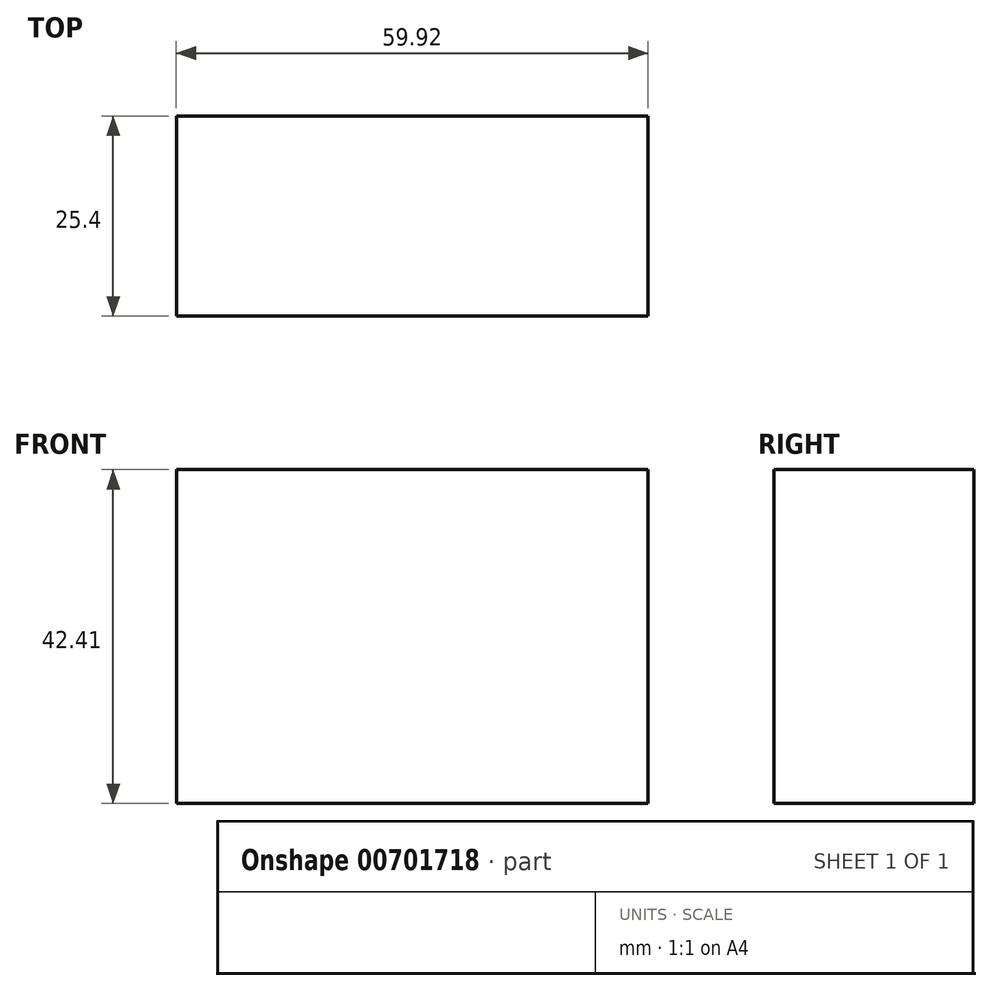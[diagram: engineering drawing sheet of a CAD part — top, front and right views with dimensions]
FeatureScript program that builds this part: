
annotation { "Feature Type Name" : "Feature", "Feature Type Description" : "" }
export const myFeature = defineFeature(function(context is Context, id is Id, definition is map)
    precondition{}
    {
        {
            var Q0;
            Q0=qCreatedBy(makeId("Front.planeOp"),FACE);
            var sketch = newSketch(context, id + "F0", { "sketchPlane" : qUnion([Q0])});
            skLineSegment(sketch, "E0.bottom", {"start": v(-95.96, 31.99) * mm, "end": v(-36.04, 31.99) * mm});
            skLineSegment(sketch, "E0.top", {"start": v(-95.96, -10.42) * mm, "end": v(-36.04, -10.42) * mm});
            skLineSegment(sketch, "E0.left", {"start": v(-95.96, 31.99) * mm, "end": v(-95.96, -10.42) * mm});
            skLineSegment(sketch, "E0.right", {"start": v(-36.04, 31.99) * mm, "end": v(-36.04, -10.42) * mm});
            skSolve(sketch);
        }
        {
            var Q0;
            Q0 = qSketchRegion(id + "F0", true);
            extrude(context, id + "F1", {"entities" : qUnion([Q0]), "depth" : 25.4 * mm, "offsetDistance" : 25.4 * mm});
        }
    });
